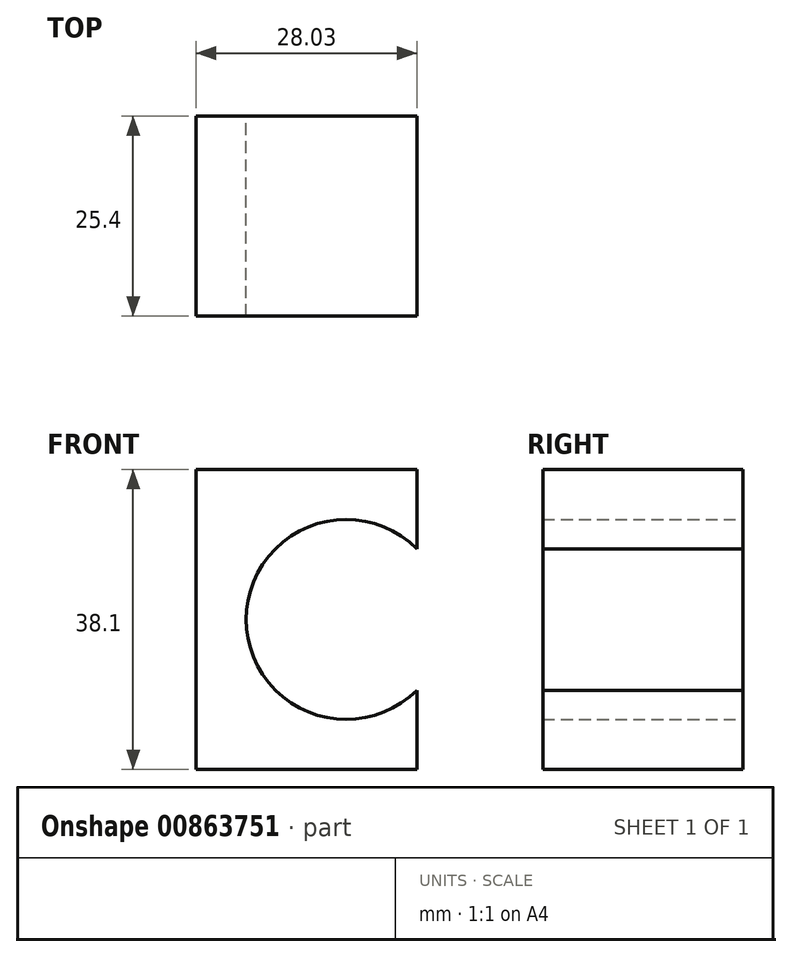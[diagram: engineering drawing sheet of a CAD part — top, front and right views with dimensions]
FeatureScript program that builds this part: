
annotation { "Feature Type Name" : "Feature", "Feature Type Description" : "" }
export const myFeature = defineFeature(function(context is Context, id is Id, definition is map)
    precondition{}
    {
        {
            var Q0;
            Q0=qCreatedBy(makeId("Front.planeOp"),FACE);
            var sketch = newSketch(context, id + "F0", { "sketchPlane" : qUnion([Q0])});
            skArc(sketch, "E0", {"start": v(8.98, 8.98) * mm, "mid": v(-12.7, 0) * mm, "end": v(8.98, -8.98) * mm});
            skLineSegment(sketch, "E1.bottom", {"start": v(8.98, -19.05) * mm, "end": v(-19.05, -19.05) * mm});
            skLineSegment(sketch, "E1.top", {"start": v(8.98, 19.05) * mm, "end": v(-19.05, 19.05) * mm});
            skLineSegment(sketch, "E1.right", {"start": v(-19.05, -19.05) * mm, "end": v(-19.05, 19.05) * mm});
            skLineSegment(sketch, "E2", {"start": v(8.98, 8.98) * mm, "end": v(8.98, 19.05) * mm});
            skLineSegment(sketch, "E3", {"start": v(8.98, -8.98) * mm, "end": v(8.98, -19.05) * mm});
            skSolve(sketch);
        }
        {
            var Q0;
            Q0=makeQuery(id+"F0.imprint","IMPRINT",FACE,{"disambiguationData":[TD([[makeQuery(id+"F0.imprint","IMPRINT",EDGE,{"derivedFrom":sQuery(id+"F0.wireOp",EDGE,"E0")}),-1.0]])]});
            extrude(context, id + "F1", {"entities" : qUnion([Q0]), "endBound" : BoundingType.SYMMETRIC, "depth" : 25.4 * mm, "offsetDistance" : 25.4 * mm});
        }
    });
